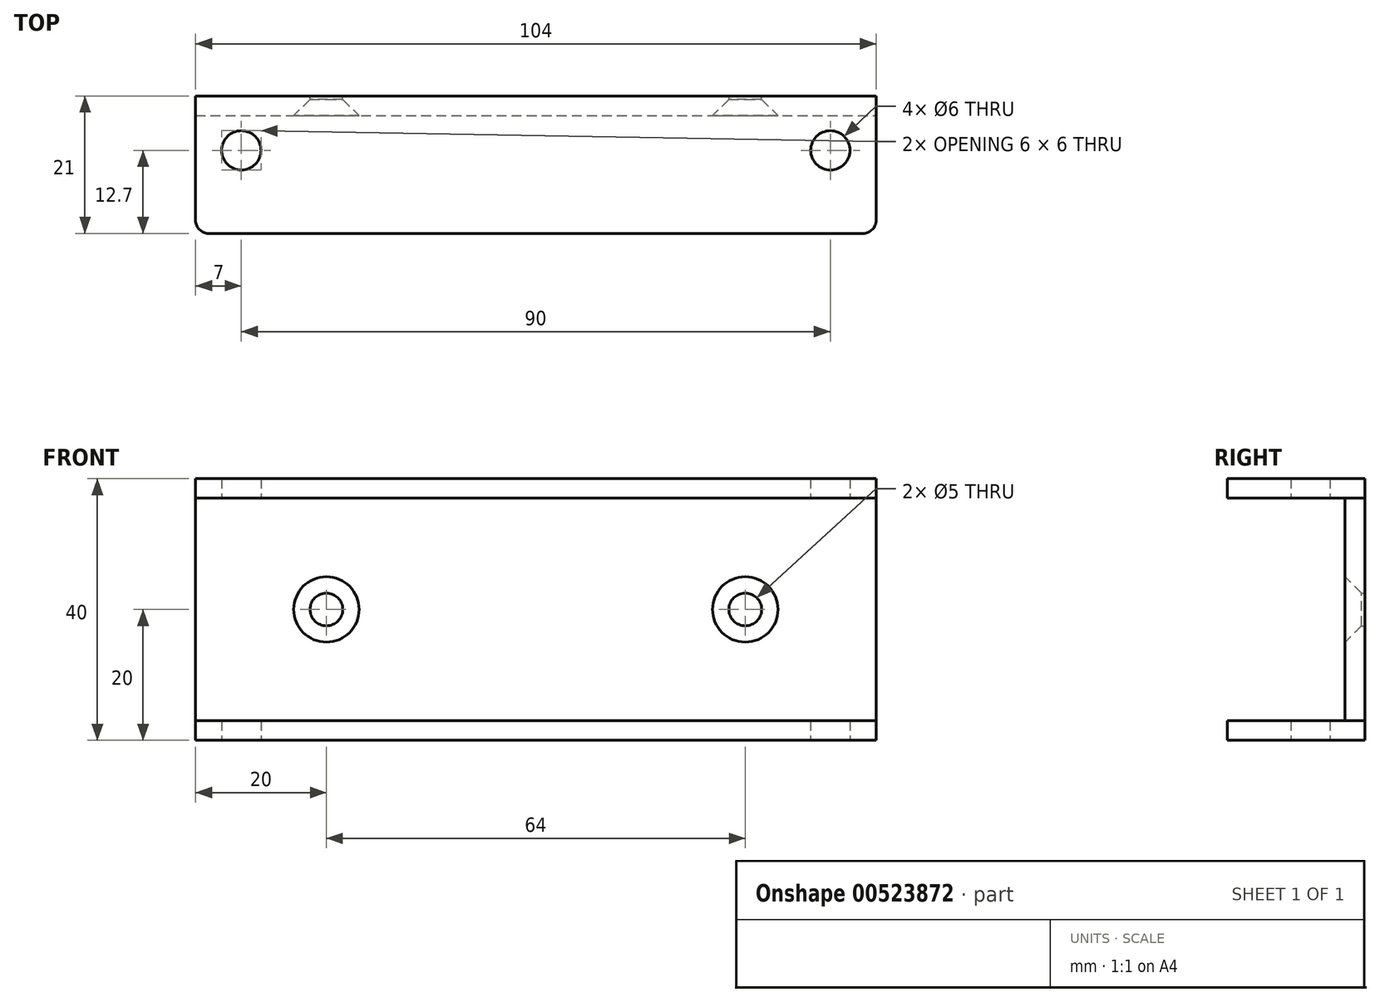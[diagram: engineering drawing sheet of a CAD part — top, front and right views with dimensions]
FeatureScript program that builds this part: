
annotation { "Feature Type Name" : "Feature", "Feature Type Description" : "" }
export const myFeature = defineFeature(function(context is Context, id is Id, definition is map)
    precondition{}
    {
        {
            var Q0;
            Q0=qCreatedBy(makeId("Front.planeOp"),FACE);
            var sketch = newSketch(context, id + "F0", { "sketchPlane" : qUnion([Q0])});
            skLineSegment(sketch, "E0.bottom", {"start": v(52, -20) * mm, "end": v(-52, -20) * mm});
            skLineSegment(sketch, "E0.top", {"start": v(52, 20) * mm, "end": v(-52, 20) * mm});
            skLineSegment(sketch, "E0.left", {"start": v(52, -20) * mm, "end": v(52, 20) * mm});
            skLineSegment(sketch, "E0.right", {"start": v(-52, -20) * mm, "end": v(-52, 20) * mm});
            skPoint(sketch, "E0.middle", {"position": v(0, 0) * mm});
            skLineSegment(sketch, "E1", {"start": v(-52, 17) * mm, "end": v(52, 17) * mm});
            skLineSegment(sketch, "E2", {"start": v(-52, -17) * mm, "end": v(52, -17) * mm});
            skCircle(sketch, "E3", {"center": v(-32, 0) * mm, "radius": 2.5 * mm});
            skCircle(sketch, "E4", {"center": v(32, 0) * mm, "radius": 2.5 * mm});
            skLineSegment(sketch, "E5.bottom", {"start": v(-52, 17) * mm, "end": v(-92, 17) * mm});
            skLineSegment(sketch, "E5.top", {"start": v(-52, -17) * mm, "end": v(-92, -17) * mm});
            skLineSegment(sketch, "E5.left", {"start": v(-52, 17) * mm, "end": v(-52, -17) * mm});
            skLineSegment(sketch, "E5.right", {"start": v(-92, 17) * mm, "end": v(-92, -17) * mm});
            skLineSegment(sketch, "E6.top", {"start": v(-52, 20) * mm, "end": v(-92, 20) * mm});
            skLineSegment(sketch, "E6.left", {"start": v(-52, 17) * mm, "end": v(-52, 20) * mm});
            skLineSegment(sketch, "E6.right", {"start": v(-92, 17) * mm, "end": v(-92, 20) * mm});
            skLineSegment(sketch, "E7.bottom", {"start": v(-92, -17) * mm, "end": v(-52, -17) * mm});
            skLineSegment(sketch, "E7.top", {"start": v(-92, -20) * mm, "end": v(-52, -20) * mm});
            skLineSegment(sketch, "E7.left", {"start": v(-92, -17) * mm, "end": v(-92, -20) * mm});
            skLineSegment(sketch, "E7.right", {"start": v(-52, -17) * mm, "end": v(-52, -20) * mm});
            skSolve(sketch);
        }
        {
            var Q0;
            {var subQ0=sQuery(id+"F0.wireOp",EDGE,"E0.top");Q0=makeQuery(id+"F0.imprint","IMPRINT",FACE,{"disambiguationData":[TD([[makeQuery(id+"F0.imprint","IMPRINT",EDGE,{"derivedFrom":subQ0}),1.0]])]});}
            var Q1;
            {var subQ0=sQuery(id+"F0.wireOp",EDGE,"E0.bottom");Q1=makeQuery(id+"F0.imprint","IMPRINT",FACE,{"disambiguationData":[TD([[makeQuery(id+"F0.imprint","IMPRINT",EDGE,{"derivedFrom":subQ0}),-1.0]])]});}
            extrude(context, id + "F1", {"entities" : qUnion([Q0, Q1]), "depth" : 21 * mm, "offsetDistance" : 25 * mm});
        }
        {
            var Q0;
            {var subQ1=sQuery(id+"F0.wireOp",EDGE,"E1");Q0=makeQuery(id+"F0.imprint","IMPRINT",FACE,{"disambiguationData":[TD([[makeQuery(id+"F0.imprint","IMPRINT",EDGE,{"derivedFrom":subQ1}),-1.0]])]});}
            extrude(context, id + "F2", {"entities" : qUnion([Q0]), "depth" : 3 * mm, "offsetDistance" : 25 * mm});
        }
        {
            var Q0;
            Q0=makeQuery(id+"F1.opExtrude","SWEPT_FACE",FACE,{"disambiguationData":[OSD([sQuery(id+"F0.wireOp",EDGE,"E0.bottom")])]});
            var sketch = newSketch(context, id + "F3", { "sketchPlane" : qUnion([Q0])});
            skCircle(sketch, "E8", {"center": v(-45, 8.3) * mm, "radius": 3 * mm});
            skCircle(sketch, "E9", {"center": v(45, 8.3) * mm, "radius": 3 * mm});
            skSolve(sketch);
        }
        {
            var Q0;
            Q0=sQuery(id+"F3.wireOp",VERTEX,"E8.center");
            var Q1;
            Q1=sQuery(id+"F3.wireOp",VERTEX,"E9.center");
            var Q2;
            Q2=makeQuery(id+"F1.opExtrude","SWEPT_BODY",BODY,{"disambiguationData":[OSD([sQuery(id+"F0.wireOp",EDGE,"E0.bottom"),sQuery(id+"F0.wireOp",EDGE,"E0.left"),sQuery(id+"F0.wireOp",EDGE,"E0.right"),sQuery(id+"F0.wireOp",EDGE,"E2")])]});
            var Q3;
            Q3=makeQuery(id+"F1.opExtrude","SWEPT_BODY",BODY,{"disambiguationData":[OSD([sQuery(id+"F0.wireOp",EDGE,"E0.top"),sQuery(id+"F0.wireOp",EDGE,"E0.left"),sQuery(id+"F0.wireOp",EDGE,"E0.right"),sQuery(id+"F0.wireOp",EDGE,"E1")])]});
            hole(context, id + "F4", {"style" : HoleStyle.SIMPLE, "endStyle" : HoleEndStyle.THROUGH, "holeDiameter" : 6 * mm, "isTappedThrough" : true, "tappedDepth" : 12 * mm, "tapClearance" : 3, "locations" : qUnion([Q0, Q1]), "scope" : qUnion([Q2, Q3])});
        }
        {
            var Q0;
            Q0=makeQuery(id+"F2.opExtrude","CAP_EDGE",EDGE,{"disambiguationData":[OSD([sQuery(id+"F0.wireOp",EDGE,"E3")])],"isStart":false});
            chamfer(context, id + "F5", {"entities" : qUnion([Q0]), "width" : 2.5 * mm, "tangentPropagation" : true});
        }
        {
            var Q0;
            Q0=makeQuery(id+"F2.opExtrude","CAP_EDGE",EDGE,{"disambiguationData":[OSD([sQuery(id+"F0.wireOp",EDGE,"E4")])],"isStart":false});
            chamfer(context, id + "F6", {"entities" : qUnion([Q0]), "width" : 2.5 * mm, "tangentPropagation" : true});
        }
        {
            var Q0;
            {var subQ0=sQuery(id+"F0.wireOp",EDGE,"E0.right");Q0=makeQuery(id+"F1.opExtrude","CAP_EDGE",EDGE,{"disambiguationData":[OSD([subQ0]),TDD([makeQuery(id+"F0.imprint","IMPRINT",EDGE,{"disambiguationData":[TD([[makeQuery(id+"F0.imprint","INTERSECT",VERTEX,{"derivedFrom":[sQuery(id+"F0.wireOp",EDGE,"E0.bottom"),subQ0]}),-1.0]])],"derivedFrom":subQ0})])],"isStart":false});}
            var Q1;
            {var subQ0=sQuery(id+"F0.wireOp",EDGE,"E0.left");Q1=makeQuery(id+"F1.opExtrude","CAP_EDGE",EDGE,{"disambiguationData":[OSD([subQ0]),TDD([makeQuery(id+"F0.imprint","IMPRINT",EDGE,{"disambiguationData":[TD([[makeQuery(id+"F0.imprint","INTERSECT",VERTEX,{"derivedFrom":[sQuery(id+"F0.wireOp",EDGE,"E0.bottom"),subQ0]}),-1.0]])],"derivedFrom":subQ0})])],"isStart":false});}
            var Q2;
            {var subQ0=sQuery(id+"F0.wireOp",EDGE,"E0.left");Q2=makeQuery(id+"F1.opExtrude","CAP_EDGE",EDGE,{"disambiguationData":[OSD([subQ0]),TDD([makeQuery(id+"F0.imprint","IMPRINT",EDGE,{"disambiguationData":[TD([[makeQuery(id+"F0.imprint","INTERSECT",VERTEX,{"derivedFrom":[sQuery(id+"F0.wireOp",EDGE,"E0.top"),subQ0]}),1.0]])],"derivedFrom":subQ0})])],"isStart":false});}
            var Q3;
            {var subQ0=sQuery(id+"F0.wireOp",EDGE,"E0.right");Q3=makeQuery(id+"F1.opExtrude","CAP_EDGE",EDGE,{"disambiguationData":[OSD([subQ0]),TDD([makeQuery(id+"F0.imprint","IMPRINT",EDGE,{"disambiguationData":[TD([[makeQuery(id+"F0.imprint","INTERSECT",VERTEX,{"derivedFrom":[sQuery(id+"F0.wireOp",EDGE,"E0.top"),subQ0]}),1.0]])],"derivedFrom":subQ0})])],"isStart":false});}
            fillet(context, id + "F7", {"entities" : qUnion([Q0, Q1, Q2, Q3]), "radius" : 2 * mm, "tangentPropagation" : true, "allowEdgeOverflow" : false});
        }
    });
